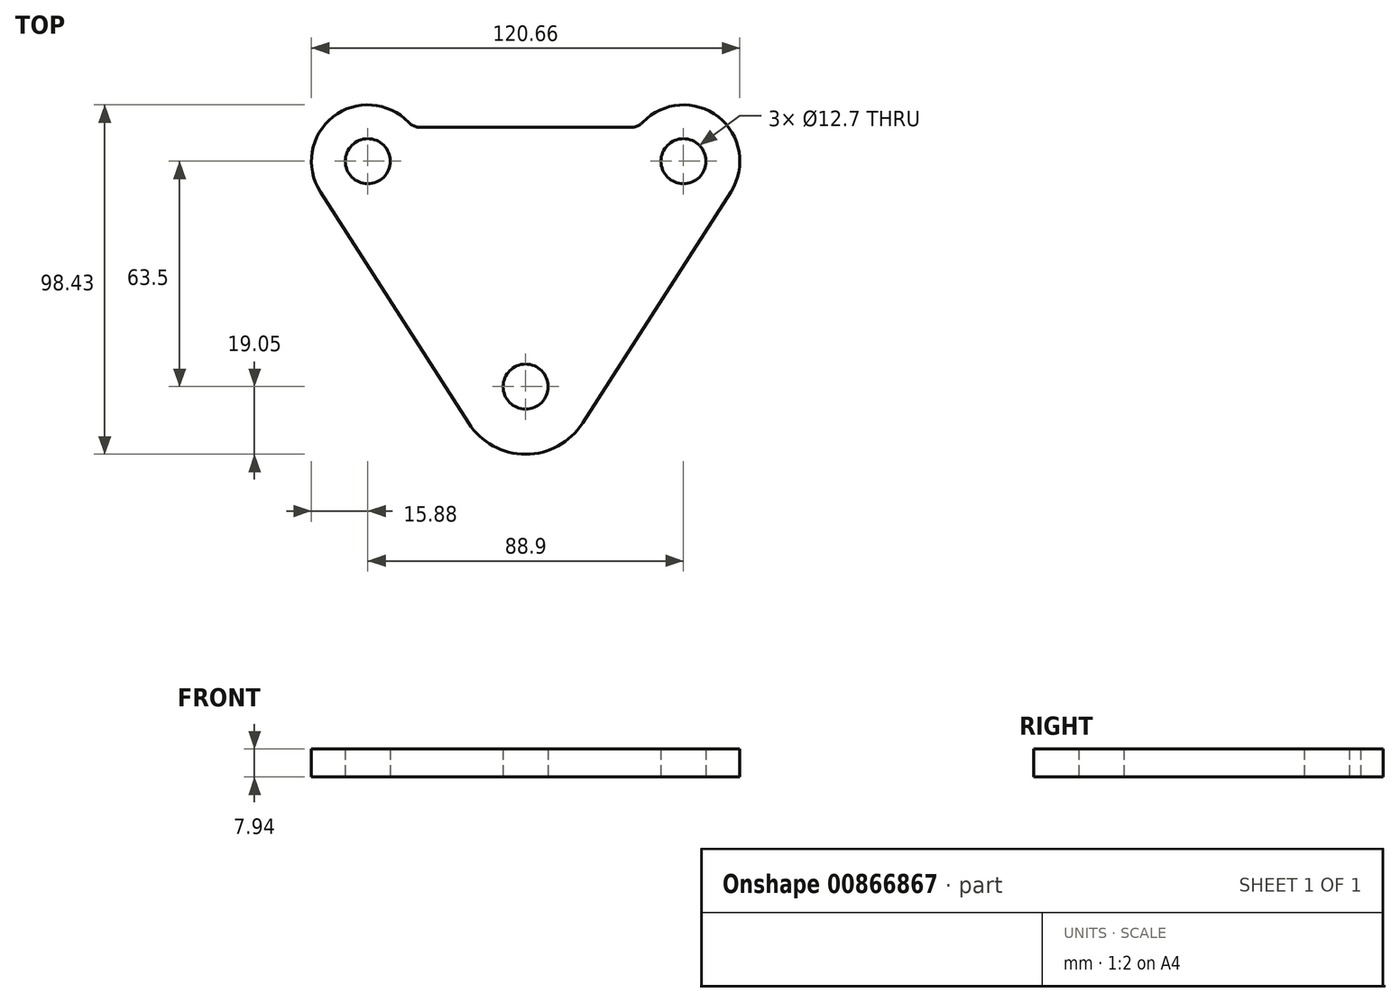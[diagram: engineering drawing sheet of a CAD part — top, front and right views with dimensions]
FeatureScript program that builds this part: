
annotation { "Feature Type Name" : "Feature", "Feature Type Description" : "" }
export const myFeature = defineFeature(function(context is Context, id is Id, definition is map)
    precondition{}
    {
        {
            var Q0;
            Q0=qCreatedBy(makeId("Top.planeOp"),FACE);
            var sketch = newSketch(context, id + "F0", { "sketchPlane" : qUnion([Q0])});
            skLineSegment(sketch, "E0", {"start": v(0, 0) * mm, "end": v(44.45, 0) * mm});
            skLineSegment(sketch, "E1", {"start": v(0, 0) * mm, "end": v(-44.45, 0) * mm});
            skCircle(sketch, "E2", {"center": v(44.45, 0) * mm, "radius": 6.35 * mm});
            skCircle(sketch, "E3", {"center": v(0, -63.5) * mm, "radius": 6.35 * mm});
            skCircle(sketch, "E4", {"center": v(-44.45, 0) * mm, "radius": 6.35 * mm});
            skCircle(sketch, "E5", {"center": v(44.45, 0) * mm, "radius": 15.88 * mm});
            skCircle(sketch, "E6", {"center": v(0, -63.5) * mm, "radius": 19.05 * mm});
            skCircle(sketch, "E7", {"center": v(-44.45, 0) * mm, "radius": 15.88 * mm});
            skLineSegment(sketch, "E8", {"start": v(57.82, -8.56) * mm, "end": v(16.04, -73.78) * mm});
            skLineSegment(sketch, "E9", {"start": v(-57.82, -8.56) * mm, "end": v(-16.04, -73.78) * mm});
            skLineSegment(sketch, "E10", {"start": v(0, -63.5) * mm, "end": v(0, 0) * mm});
            skArc(sketch, "E11", {"start": v(29.56, 9.52) * mm, "mid": v(31.43, 9.9) * mm, "end": v(33, 11) * mm});
            skArc(sketch, "E12", {"start": v(-33, 11) * mm, "mid": v(-31.43, 9.9) * mm, "end": v(-29.56, 9.53) * mm});
            skLineSegment(sketch, "E13", {"start": v(29.56, 9.53) * mm, "end": v(-29.56, 9.53) * mm});
            skSolve(sketch);
        }
        {
            var Q0;
            Q0 = qSketchRegion(id + "F0", true);
            extrude(context, id + "F1", {"entities" : qUnion([Q0]), "depth" : 7.94 * mm, "offsetDistance" : 25.4 * mm});
        }
    });
